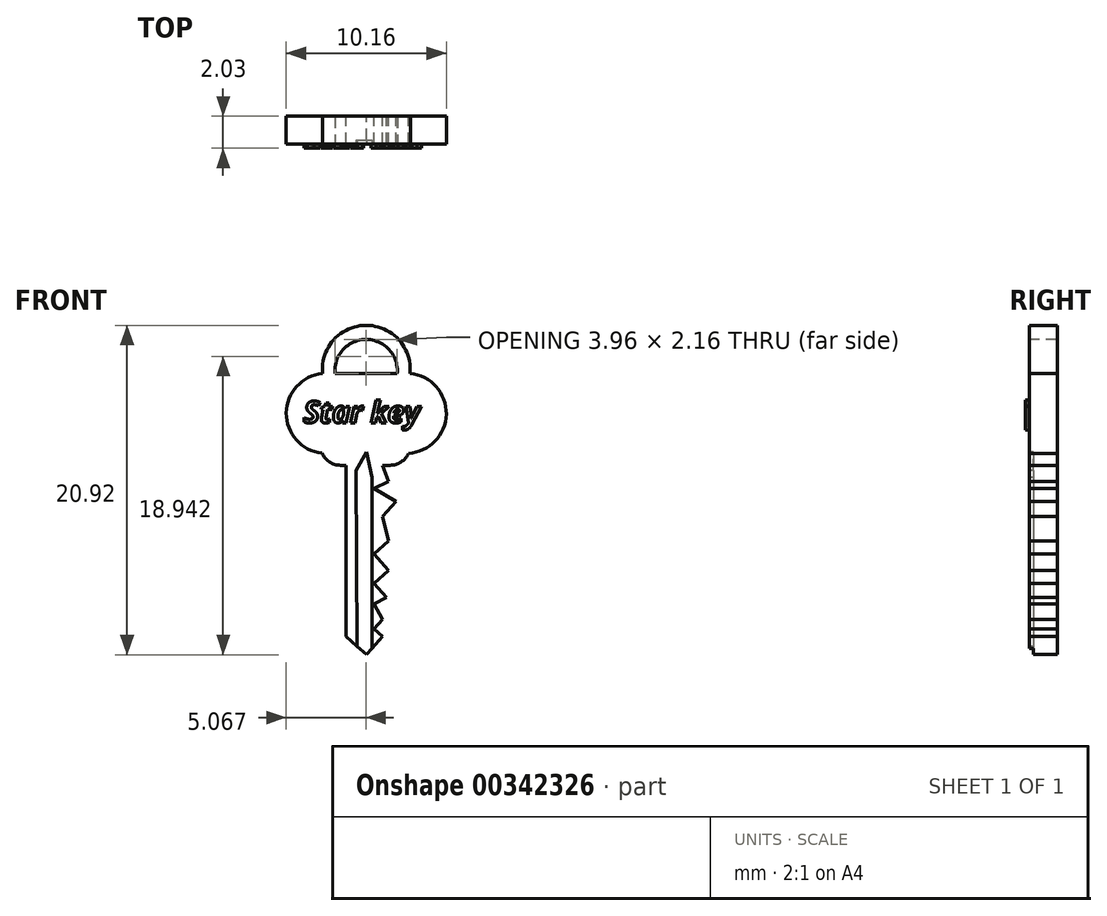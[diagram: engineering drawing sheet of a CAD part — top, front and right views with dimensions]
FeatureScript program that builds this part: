
annotation { "Feature Type Name" : "Feature", "Feature Type Description" : "" }
export const myFeature = defineFeature(function(context is Context, id is Id, definition is map)
    precondition{}
    {
        {
            var Q0;
            Q0=qCreatedBy(makeId("Front.planeOp"),FACE);
            var sketch = newSketch(context, id + "F0", { "sketchPlane" : qUnion([Q0])});
            skCircle(sketch, "E0", {"center": v(0, 2.8) * mm, "radius": 2.8 * mm});
            skCircle(sketch, "E1", {"center": v(-2.54, 0) * mm, "radius": 2.54 * mm});
            skCircle(sketch, "E2", {"center": v(2.54, 0) * mm, "radius": 2.54 * mm});
            skLineSegment(sketch, "E3", {"start": v(-2.81, -2.53) * mm, "end": v(-2.81, -3.3) * mm});
            skLineSegment(sketch, "E4", {"start": v(-2.81, -3.3) * mm, "end": v(-1.27, -3.3) * mm});
            skLineSegment(sketch, "E5", {"start": v(-1.27, -3.3) * mm, "end": v(-1.27, -14.18) * mm});
            skLineSegment(sketch, "E6", {"start": v(-1.27, -14.18) * mm, "end": v(0, -15.33) * mm});
            skLineSegment(sketch, "E7", {"start": v(0, -15.33) * mm, "end": v(1.03, -14.18) * mm});
            skLineSegment(sketch, "E8", {"start": v(1.03, -3.3) * mm, "end": v(2.68, -3.3) * mm});
            skLineSegment(sketch, "E9", {"start": v(2.68, -3.3) * mm, "end": v(2.68, -2.54) * mm});
            skLineSegment(sketch, "E10", {"start": v(1.03, -14.18) * mm, "end": v(0.49, -13.7) * mm});
            skLineSegment(sketch, "E11", {"start": v(0.49, -13.7) * mm, "end": v(1.03, -13.1) * mm});
            skLineSegment(sketch, "E12", {"start": v(1.03, -13.1) * mm, "end": v(0.49, -12.12) * mm});
            skLineSegment(sketch, "E13", {"start": v(0.49, -12.12) * mm, "end": v(1.28, -11.68) * mm});
            skLineSegment(sketch, "E14", {"start": v(1.28, -11.68) * mm, "end": v(0.49, -10.8) * mm});
            skLineSegment(sketch, "E15", {"start": v(0.49, -10.8) * mm, "end": v(1.42, -9.97) * mm});
            skLineSegment(sketch, "E16", {"start": v(1.42, -9.97) * mm, "end": v(0.49, -8.93) * mm});
            skLineSegment(sketch, "E17", {"start": v(0.49, -8.93) * mm, "end": v(1.42, -8.1) * mm});
            skLineSegment(sketch, "E18", {"start": v(1.42, -8.1) * mm, "end": v(1.03, -6.56) * mm});
            skPoint(sketch, "E19.end.orphan", {"position": v(0.49, -4.33) * mm});
            skPoint(sketch, "E20.end.orphan", {"position": v(1.42, -5.59) * mm});
            skLineSegment(sketch, "E21", {"start": v(1.03, -6.56) * mm, "end": v(1.88, -5.59) * mm});
            skLineSegment(sketch, "E22", {"start": v(1.88, -5.59) * mm, "end": v(0.49, -4.76) * mm});
            skLineSegment(sketch, "E23", {"start": v(0.49, -4.76) * mm, "end": v(1.42, -4.33) * mm});
            skLineSegment(sketch, "E24", {"start": v(1.42, -4.33) * mm, "end": v(1.03, -3.3) * mm});
            skSolve(sketch);
        }
        {
            var Q0;
            {var subQ1=sQuery(id+"F0.wireOp",EDGE,"E3");Q0=makeQuery(id+"F0.imprint","IMPRINT",FACE,{"disambiguationData":[TD([[makeQuery(id+"F0.imprint","IMPRINT",EDGE,{"derivedFrom":subQ1}),1.0]])]});}
            var Q1;
            {var subQ0=sQuery(id+"F0.wireOp",EDGE,"E1");var subQ4=makeQuery(id+"F0.imprint","INTERSECT",VERTEX,{"derivedFrom":[subQ0,sQuery(id+"F0.wireOp",EDGE,"E3")]});Q1=makeQuery(id+"F0.imprint","IMPRINT",FACE,{"disambiguationData":[TD([[makeQuery(id+"F0.imprint","IMPRINT",EDGE,{"disambiguationData":[TD([[subQ4,1.0]])],"derivedFrom":subQ0}),1.0]])]});}
            var Q2;
            {var subQ0=sQuery(id+"F0.wireOp",EDGE,"E1");var subQ1=sQuery(id+"F0.wireOp",EDGE,"E0");var subQ2=makeQuery(id+"F0.imprint","INTERSECT",VERTEX,{"derivedFrom":[subQ1,subQ0]});Q2=makeQuery(id+"F0.imprint","IMPRINT",FACE,{"disambiguationData":[TD([[makeQuery(id+"F0.imprint","IMPRINT",EDGE,{"disambiguationData":[TD([[subQ2,1.0]])],"derivedFrom":subQ1}),1.0]])]});}
            var Q3;
            {var subQ0=sQuery(id+"F0.wireOp",EDGE,"E2");var subQ4=makeQuery(id+"F0.imprint","INTERSECT",VERTEX,{"derivedFrom":[subQ0,sQuery(id+"F0.wireOp",EDGE,"E9")]});Q3=makeQuery(id+"F0.imprint","IMPRINT",FACE,{"disambiguationData":[TD([[makeQuery(id+"F0.imprint","IMPRINT",EDGE,{"disambiguationData":[TD([[subQ4,-1.0]])],"derivedFrom":subQ0}),1.0]])]});}
            var Q4;
            {var subQ0=sQuery(id+"F0.wireOp",EDGE,"E2");var subQ1=sQuery(id+"F0.wireOp",EDGE,"E0");var subQ2=makeQuery(id+"F0.imprint","INTERSECT",VERTEX,{"derivedFrom":[subQ1,subQ0]});Q4=makeQuery(id+"F0.imprint","IMPRINT",FACE,{"disambiguationData":[TD([[makeQuery(id+"F0.imprint","IMPRINT",EDGE,{"disambiguationData":[TD([[subQ2,1.0]])],"derivedFrom":subQ1}),1.0]])]});}
            var Q5;
            {var subQ0=sQuery(id+"F0.wireOp",EDGE,"E1");var subQ1=sQuery(id+"F0.wireOp",EDGE,"E0");var subQ2=makeQuery(id+"F0.imprint","INTERSECT",VERTEX,{"derivedFrom":[subQ1,subQ0]});Q5=makeQuery(id+"F0.imprint","IMPRINT",FACE,{"disambiguationData":[TD([[makeQuery(id+"F0.imprint","IMPRINT",EDGE,{"disambiguationData":[TD([[subQ2,-1.0]])],"derivedFrom":subQ1}),1.0]])]});}
            extrude(context, id + "F1", {"entities" : qUnion([Q0, Q1, Q2, Q3, Q4, Q5]), "depth" : 1.78 * mm});
        }
        {
            var Q0;
            Q0=makeQuery(id+"F1.opExtrude","SWEPT_EDGE",EDGE,{"disambiguationData":[OSD([sQuery(id+"F0.wireOp",EDGE,"E3"),sQuery(id+"F0.wireOp",EDGE,"E4")])]});
            var Q1;
            Q1=makeQuery(id+"F1.opExtrude","SWEPT_EDGE",EDGE,{"disambiguationData":[OSD([sQuery(id+"F0.wireOp",EDGE,"E8"),sQuery(id+"F0.wireOp",EDGE,"E9")])]});
            fillet(context, id + "F2", {"entities" : qUnion([Q0, Q1]), "radius" : 1.27 * mm, "tangentPropagation" : true, "allowEdgeOverflow" : false});
        }
        {
            var Q0;
            Q0=makeQuery(id+"F1.opExtrude","CAP_FACE",FACE,{"disambiguationData":[OSD([sQuery(id+"F0.wireOp",EDGE,"E0"),sQuery(id+"F0.wireOp",EDGE,"E1"),sQuery(id+"F0.wireOp",EDGE,"E2"),sQuery(id+"F0.wireOp",EDGE,"E3"),sQuery(id+"F0.wireOp",EDGE,"E4"),sQuery(id+"F0.wireOp",EDGE,"E5"),sQuery(id+"F0.wireOp",EDGE,"E6"),sQuery(id+"F0.wireOp",EDGE,"E7"),sQuery(id+"F0.wireOp",EDGE,"E8"),sQuery(id+"F0.wireOp",EDGE,"E9"),sQuery(id+"F0.wireOp",EDGE,"E10"),sQuery(id+"F0.wireOp",EDGE,"E11"),sQuery(id+"F0.wireOp",EDGE,"E12"),sQuery(id+"F0.wireOp",EDGE,"E13"),sQuery(id+"F0.wireOp",EDGE,"E14"),sQuery(id+"F0.wireOp",EDGE,"E15"),sQuery(id+"F0.wireOp",EDGE,"E16"),sQuery(id+"F0.wireOp",EDGE,"E17"),sQuery(id+"F0.wireOp",EDGE,"E18"),sQuery(id+"F0.wireOp",EDGE,"E21"),sQuery(id+"F0.wireOp",EDGE,"E22"),sQuery(id+"F0.wireOp",EDGE,"E23"),sQuery(id+"F0.wireOp",EDGE,"E24")])],"isStart":false});
            var sketch = newSketch(context, id + "F3", { "sketchPlane" : qUnion([Q0])});
            skArc(sketch, "E25", {"start": v(6.47, 2.53) * mm, "mid": v(0.04, 8.96) * mm, "end": v(-6.38, 2.53) * mm});
            skLineSegment(sketch, "E26", {"start": v(-6.38, 2.53) * mm, "end": v(6.47, 2.53) * mm});
            skSolve(sketch);
        }
        {
            var Q0;
            {var subQ1=makeQuery(id+"F1.opExtrude","CAP_EDGE",EDGE,{"disambiguationData":[OSD([sQuery(id+"F0.wireOp",EDGE,"E0")])],"isStart":false});Q0=makeQuery(id+"F3.imprint","IMPRINT",FACE,{"disambiguationData":[TD([[makeQuery(id+"F3.imprint","IMPRINT",EDGE,{"derivedFrom":subQ1}),1.0]])]});}
            var sketch = newSketch(context, id + "F4", { "sketchPlane" : qUnion([Q0])});
            skArc(sketch, "E27", {"start": v(1.97, 2.53) * mm, "mid": v(-0.01, 4.7) * mm, "end": v(-2, 2.53) * mm});
            skLineSegment(sketch, "E28", {"start": v(-2, 2.53) * mm, "end": v(1.97, 2.53) * mm});
            skSolve(sketch);
        }
        {
            var Q0;
            Q0 = qSketchRegion(id + "F4", true);
            extrude(context, id + "F5", {"entities" : qUnion([Q0]), "operationType" : NewBodyOperationType.REMOVE, "oppositeDirection" : true, "depth" : 12.7 * mm});
        }
        {
            var Q0;
            {var subQ21=sQuery(id+"F0.wireOp",EDGE,"E1");var subQ25=makeQuery(id+"F1.opExtrude","CAP_EDGE",EDGE,{"disambiguationData":[OSD([subQ21])],"isStart":false});Q0=makeQuery(id+"F3.imprint","IMPRINT",FACE,{"disambiguationData":[TD([[makeQuery(id+"F3.imprint","IMPRINT",EDGE,{"derivedFrom":subQ25}),1.0]])]});}
            var sketch = newSketch(context, id + "F6", { "sketchPlane" : qUnion([Q0])});
            skText(sketch, "E29", { "text": "Star key", "fontName": "NotoSans-BoldItalic.ttf"});
            const initialGuessF6  = {"E29": [-0.00398, -0.0006, 1, 0, 0.00138]};
            skSetInitialGuess(sketch, initialGuessF6);
            skSolve(sketch);
        }
        {
            var Q0;
            Q0 = qSketchRegion(id + "F6", true);
            extrude(context, id + "F7", {"entities" : qUnion([Q0]), "operationType" : NewBodyOperationType.ADD, "depth" : 0.25 * mm});
        }
        {
            var Q0;
            {var subQ21=sQuery(id+"F0.wireOp",EDGE,"E1");var subQ25=makeQuery(id+"F1.opExtrude","CAP_EDGE",EDGE,{"disambiguationData":[OSD([subQ21])],"isStart":false});Q0=makeQuery(id+"F3.imprint","IMPRINT",FACE,{"disambiguationData":[TD([[makeQuery(id+"F3.imprint","IMPRINT",EDGE,{"derivedFrom":subQ25}),1.0]])]});}
            var sketch = newSketch(context, id + "F8", { "sketchPlane" : qUnion([Q0])});
            skLineSegment(sketch, "E30", {"start": v(52.25, 18.58) * mm, "end": v(52.25, 18.58) * mm});
            skLineSegment(sketch, "E31", {"start": v(46.45, 17.1) * mm, "end": v(46.45, 17.1) * mm});
            skLineSegment(sketch, "E32", {"start": v(-0.56, -14.98) * mm, "end": v(0, -15.62) * mm});
            skLineSegment(sketch, "E33", {"start": v(0.38, -15.62) * mm, "end": v(0, -15.62) * mm});
            skLineSegment(sketch, "E34", {"start": v(0.36, -3.1) * mm, "end": v(0.36, -16.32) * mm});
            skLineSegment(sketch, "E35", {"start": v(-0.65, -3) * mm, "end": v(-0.56, -16.43) * mm});
            skLineSegment(sketch, "E36", {"start": v(-0.65, -3.64) * mm, "end": v(0, -2.47) * mm});
            skLineSegment(sketch, "E37", {"start": v(0, -2.47) * mm, "end": v(0.36, -4.08) * mm});
            skLineSegment(sketch, "E38", {"start": v(-0.56, -16.43) * mm, "end": v(0.36, -16.32) * mm});
            skSolve(sketch);
        }
        {
            var Q0;
            {var subQ0=sQuery(id+"F8.wireOp",EDGE,"E36");Q0=makeQuery(id+"F8.imprint","IMPRINT",FACE,{"disambiguationData":[TD([[makeQuery(id+"F8.imprint","IMPRINT",EDGE,{"derivedFrom":subQ0}),-1.0]])]});}
            extrude(context, id + "F9", {"entities" : qUnion([Q0]), "operationType" : NewBodyOperationType.REMOVE, "oppositeDirection" : true, "depth" : 0.25 * mm});
        }
    });
